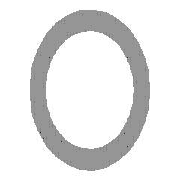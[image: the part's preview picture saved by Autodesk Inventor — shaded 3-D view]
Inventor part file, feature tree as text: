
AUTODESK INVENTOR PART (.ipt)
format: ipt  version: 2021 (Build 250183000, 183)  size: 376,320 bytes
history: native  units: mm (DEFAULTED — no unit token found)
features: other x5, plane x2, sketch x2, sweep x1
ambient origin geometry x8: Origin, YZ Plane, XZ Plane, XY Plane, X Axis, Y Axis, Z Axis, Center Point
bodies: Solid1 (feature_tree)
feature tree (10):
  parser-record x1  (decoder bookkeeping rows leaked as tree rows — omitted from the tree; the rows remain in map.json)
  other  "Driven Length"
  other  "Plano inicial"
  other  "Plano final"
  other  "Trayectoria de barrido"
  plane  "Plano de trabajo de orientación"
  sweep  "Cuerpo"
  sketch  "Sketch3"  dims[d0=42.164mm d1=3.556mm]
  plane  "Work Plane3"
  sketch  "Sketch4"  dims[d4=-0.0mm d5=1194.403192mm d6=90.0deg d7=1194.403192mm d8=0.0mm d9=0.0mm d22=16.002mm d23=53.080004mm d36=231.902mm]
